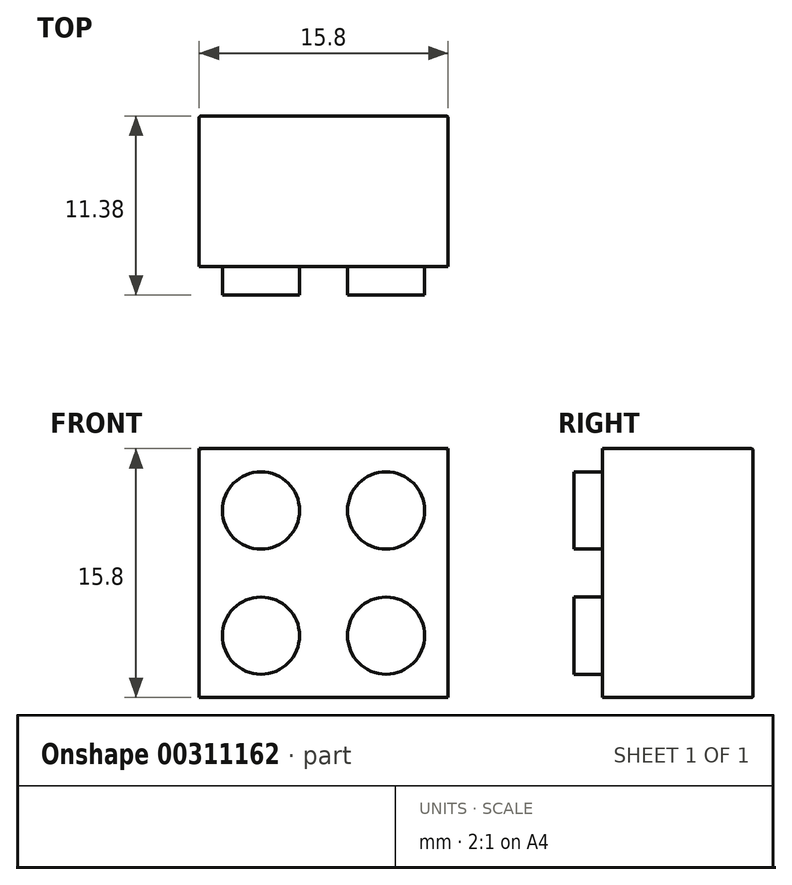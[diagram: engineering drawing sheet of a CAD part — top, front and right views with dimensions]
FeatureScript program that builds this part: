
annotation { "Feature Type Name" : "Feature", "Feature Type Description" : "" }
export const myFeature = defineFeature(function(context is Context, id is Id, definition is map)
    precondition{}
    {
        {
            var Q0;
            Q0=qCreatedBy(makeId("Front.planeOp"),FACE);
            var sketch = newSketch(context, id + "F0", { "sketchPlane" : qUnion([Q0])});
            skLineSegment(sketch, "E0.bottom", {"start": v(0, 15.8) * mm, "end": v(15.8, 15.8) * mm});
            skLineSegment(sketch, "E0.top", {"start": v(0, 0) * mm, "end": v(15.8, 0) * mm});
            skLineSegment(sketch, "E0.left", {"start": v(0, 15.8) * mm, "end": v(0, 0) * mm});
            skLineSegment(sketch, "E0.right", {"start": v(15.8, 15.8) * mm, "end": v(15.8, 0) * mm});
            skSolve(sketch);
        }
        {
            var Q0;
            Q0 = qSketchRegion(id + "F0", true);
            extrude(context, id + "F1", {"entities" : qUnion([Q0]), "depth" : 9.55 * mm});
        }
        {
            var Q0;
            Q0=makeQuery(id+"F1.opExtrude","CAP_FACE",FACE,{"disambiguationData":[OSD([sQuery(id+"F0.wireOp",EDGE,"E0.bottom"),sQuery(id+"F0.wireOp",EDGE,"E0.top"),sQuery(id+"F0.wireOp",EDGE,"E0.left"),sQuery(id+"F0.wireOp",EDGE,"E0.right")])],"isStart":false});
            var sketch = newSketch(context, id + "F2", { "sketchPlane" : qUnion([Q0])});
            skCircle(sketch, "E1", {"center": v(3.93, 11.88) * mm, "radius": 2.45 * mm});
            skCircle(sketch, "E2", {"center": v(11.88, 11.88) * mm, "radius": 2.45 * mm});
            skCircle(sketch, "E3", {"center": v(11.88, 3.93) * mm, "radius": 2.45 * mm});
            skCircle(sketch, "E4", {"center": v(3.93, 3.93) * mm, "radius": 2.45 * mm});
            skSolve(sketch);
        }
        {
            var Q0;
            Q0=makeQuery(id+"F2.imprint","IMPRINT",FACE,{"disambiguationData":[TD([[makeQuery(id+"F2.imprint","IMPRINT",EDGE,{"derivedFrom":sQuery(id+"F2.wireOp",EDGE,"E1")}),-1.0]])]});
            var sketch = newSketch(context, id + "F3", { "sketchPlane" : qUnion([Q0])});
            skSolve(sketch);
        }
        {
            var Q0;
            Q0 = qSketchRegion(id + "F3", true);
            var Q1;
            Q1=makeQuery(id+"F2.imprint","IMPRINT",FACE,{"disambiguationData":[TD([[makeQuery(id+"F2.imprint","IMPRINT",EDGE,{"derivedFrom":sQuery(id+"F2.wireOp",EDGE,"E1")}),1.0]])]});
            extrude(context, id + "F4", {"entities" : qUnion([Q0, Q1]), "operationType" : NewBodyOperationType.ADD, "depth" : 1.83 * mm});
        }
        {
            var Q0;
            Q0=makeQuery(id+"F3.imprint","IMPRINT",FACE,{"disambiguationData":[TD([[makeQuery(id+"F3.imprint","IMPRINT",EDGE,{"derivedFrom":makeQuery(id+"F2.imprint","IMPRINT",EDGE,{"derivedFrom":sQuery(id+"F2.wireOp",EDGE,"E1")})}),-1.0]])]});
            var sketch = newSketch(context, id + "F5", { "sketchPlane" : qUnion([Q0])});
            skSolve(sketch);
        }
        {
            var Q0;
            Q0 = qSketchRegion(id + "F5", true);
            var Q1;
            Q1=makeQuery(id+"F3.imprint","IMPRINT",FACE,{"disambiguationData":[TD([[makeQuery(id+"F3.imprint","IMPRINT",EDGE,{"derivedFrom":makeQuery(id+"F2.imprint","IMPRINT",EDGE,{"derivedFrom":sQuery(id+"F2.wireOp",EDGE,"E2")})}),1.0]])]});
            var Q2;
            Q2=makeQuery(id+"F3.imprint","IMPRINT",FACE,{"disambiguationData":[TD([[makeQuery(id+"F3.imprint","IMPRINT",EDGE,{"derivedFrom":makeQuery(id+"F2.imprint","IMPRINT",EDGE,{"derivedFrom":sQuery(id+"F2.wireOp",EDGE,"E4")})}),1.0]])]});
            var Q3;
            Q3=makeQuery(id+"F3.imprint","IMPRINT",FACE,{"disambiguationData":[TD([[makeQuery(id+"F3.imprint","IMPRINT",EDGE,{"derivedFrom":makeQuery(id+"F2.imprint","IMPRINT",EDGE,{"derivedFrom":sQuery(id+"F2.wireOp",EDGE,"E3")})}),1.0]])]});
            extrude(context, id + "F6", {"entities" : qUnion([Q0, Q1, Q2, Q3]), "operationType" : NewBodyOperationType.ADD, "depth" : 1.83 * mm});
        }
        {
            var Q0;
            Q0=makeQuery(id+"F1.opExtrude","CAP_FACE",FACE,{"disambiguationData":[OSD([sQuery(id+"F0.wireOp",EDGE,"E0.bottom"),sQuery(id+"F0.wireOp",EDGE,"E0.top"),sQuery(id+"F0.wireOp",EDGE,"E0.left"),sQuery(id+"F0.wireOp",EDGE,"E0.right")])],"isStart":true});
            fillet(context, id + "F7", {"entities" : qUnion([Q0]), "radius" : 0.1 * mm, "tangentPropagation" : true, "allowEdgeOverflow" : false});
        }
    });
